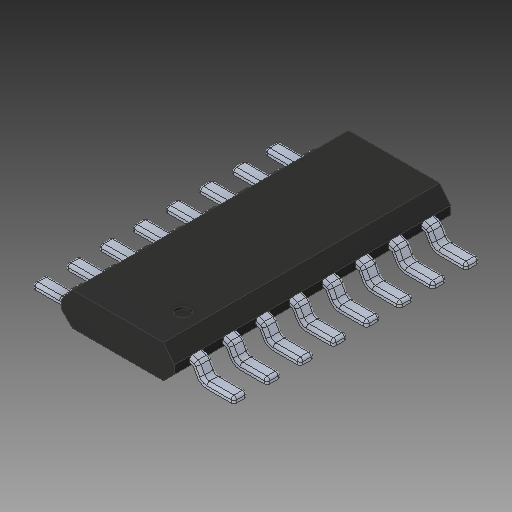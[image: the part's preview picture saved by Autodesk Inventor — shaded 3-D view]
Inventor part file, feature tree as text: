
AUTODESK INVENTOR PART (.ipt)
format: ipt  version: 2018.3 (Build 223284000, 284)  size: 657,920 bytes
history: native  units: mm
features: other x25, mirror x8, fillet x1
ambient origin geometry x8: Origin, YZ Plane, XZ Plane, XY Plane, X Axis, Y Axis, Z Axis, Center Point
bodies: Body1 (feature_tree), Body2 (feature_tree), Body3 (feature_tree), Body4 (feature_tree), Body5 (feature_tree), Body6 (feature_tree), Body7 (feature_tree), Body8 (feature_tree), Body9 (feature_tree), Body10 (feature_tree), Body11 (feature_tree), Body12 (feature_tree), Body13 (feature_tree), Body14 (feature_tree), Body15 (feature_tree), Body16 (feature_tree), Body17 (feature_tree)
feature tree (34):
  other  "Sólido1"
  other  "Sólido2"
  other  "Sólido3"
  other  "Sólido4"
  other  "Sólido5"
  other  "Sólido6"
  other  "Sólido7"
  other  "Sólido8"
  other  "Sólido9"
  other  "Sólido10"
  other  "Sólido11"
  other  "Sólido12"
  other  "Sólido13"
  other  "Sólido14"
  other  "Sólido15"
  other  "Sólido16"
  other  "Sólido17"
  fillet  "Fillet1"  [1 undecoded]
  other  "LPattern1[1]"
  other  "LPattern1[2]"
  other  "LPattern1[3]"
  mirror  "Mirror1[1]"
  mirror  "Mirror1[2]"
  mirror  "Mirror1[3]"
  mirror  "Mirror1[4]"
  other  "LPattern1[4]"
  other  "LPattern1[5]"
  other  "LPattern1[6]"
  mirror  "Mirror1[5]"
  mirror  "Mirror1[6]"
  mirror  "Mirror1[7]"
  other  "Cut-Extrude1"
  other  "LPattern1[7]"
  mirror  "Mirror1[8]"
note: 1 required parameter value undecoded (feature->parameter linkage not recoverable at this tier; creation-order binding heuristic only, values carry confidence <= 0.55)
